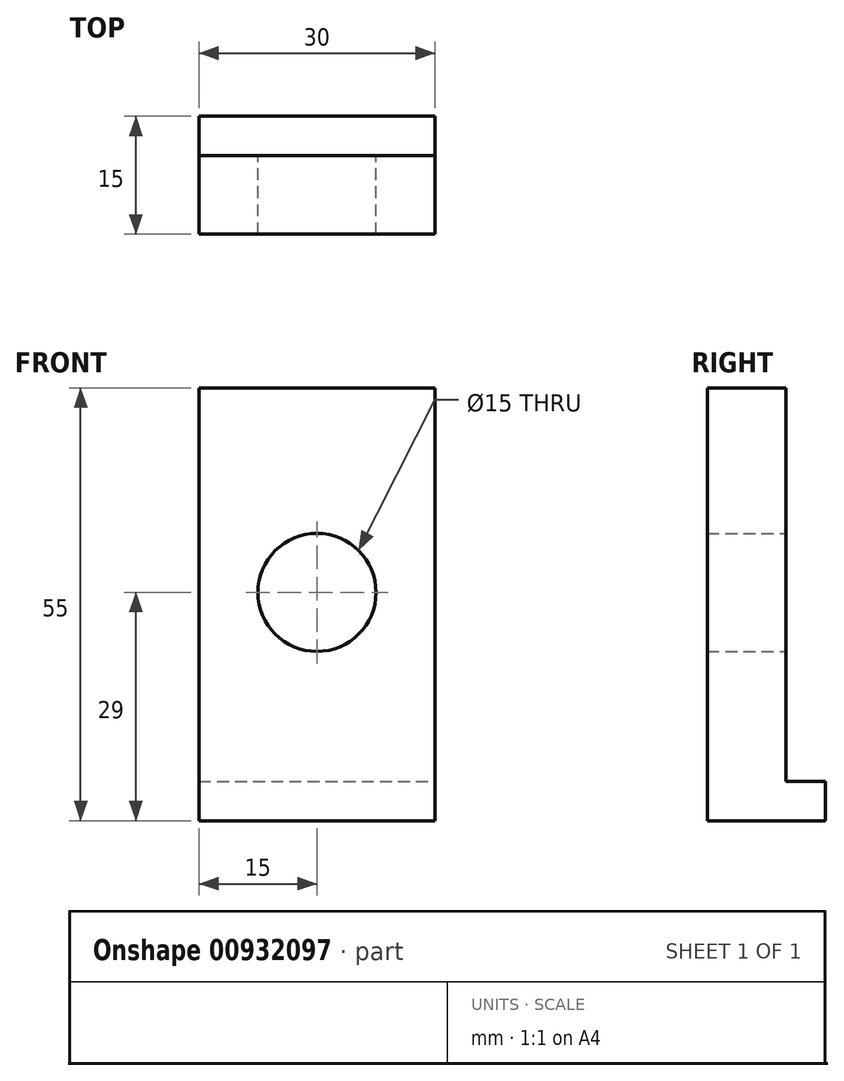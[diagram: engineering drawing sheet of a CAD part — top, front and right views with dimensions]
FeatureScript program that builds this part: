
annotation { "Feature Type Name" : "Feature", "Feature Type Description" : "" }
export const myFeature = defineFeature(function(context is Context, id is Id, definition is map)
    precondition{}
    {
        {
            var Q0;
            Q0=qCreatedBy(makeId("Front.planeOp"),FACE);
            var sketch = newSketch(context, id + "F0", { "sketchPlane" : qUnion([Q0])});
            skLineSegment(sketch, "E0.bottom", {"start": v(15, -25) * mm, "end": v(-15, -25) * mm});
            skLineSegment(sketch, "E0.top", {"start": v(15, 25) * mm, "end": v(-15, 25) * mm});
            skLineSegment(sketch, "E0.left", {"start": v(15, -25) * mm, "end": v(15, 25) * mm});
            skLineSegment(sketch, "E0.right", {"start": v(-15, -25) * mm, "end": v(-15, 25) * mm});
            skPoint(sketch, "E0.middle", {"position": v(0, 0) * mm});
            skCircle(sketch, "E1", {"center": v(0, -1) * mm, "radius": 7.5 * mm});
            skLineSegment(sketch, "E2", {"start": v(-15, -25) * mm, "end": v(-15, -30) * mm});
            skLineSegment(sketch, "E3", {"start": v(-15, -30) * mm, "end": v(15, -30) * mm});
            skLineSegment(sketch, "E4", {"start": v(15, -30) * mm, "end": v(15, -25) * mm});
            skSolve(sketch);
        }
        {
            var Q0;
            Q0=makeQuery(id+"F0.imprint","IMPRINT",FACE,{"disambiguationData":[TD([[makeQuery(id+"F0.imprint","IMPRINT",EDGE,{"derivedFrom":sQuery(id+"F0.wireOp",EDGE,"E0.bottom")}),-1.0]])]});
            var Q1;
            Q1=makeQuery(id+"F0.imprint","IMPRINT",FACE,{"disambiguationData":[TD([[makeQuery(id+"F0.imprint","IMPRINT",EDGE,{"derivedFrom":sQuery(id+"F0.wireOp",EDGE,"E0.bottom")}),1.0]])]});
            var Q2;
            Q2 = qSketchRegion(id + "F2", true);
            extrude(context, id + "F1", {"entities" : qUnion([Q0, Q1, Q2]), "depth" : 10 * mm, "offsetDistance" : 25.4 * mm});
        }
        {
            var Q0;
            Q0=makeQuery(id+"F1.opExtrude","CAP_FACE",FACE,{"disambiguationData":[OSD([sQuery(id+"F0.wireOp",EDGE,"E0.bottom"),sQuery(id+"F0.wireOp",EDGE,"E0.top"),sQuery(id+"F0.wireOp",EDGE,"E0.left"),sQuery(id+"F0.wireOp",EDGE,"E0.right"),sQuery(id+"F0.wireOp",EDGE,"E1")])],"isStart":true});
            var sketch = newSketch(context, id + "F2", { "sketchPlane" : qUnion([Q0])});
            skLineSegment(sketch, "E5.bottom", {"start": v(15, -30) * mm, "end": v(-15, -30) * mm});
            skLineSegment(sketch, "E5.top", {"start": v(15, -25) * mm, "end": v(-15, -25) * mm});
            skLineSegment(sketch, "E5.left", {"start": v(15, -30) * mm, "end": v(15, -25) * mm});
            skLineSegment(sketch, "E5.right", {"start": v(-15, -30) * mm, "end": v(-15, -25) * mm});
            skSolve(sketch);
        }
        {
            var Q0;
            Q0 = qSketchRegion(id + "F2", true);
            var Q1;
            Q1=makeQuery(id+"F1.opExtrude","CAP_FACE",FACE,{"disambiguationData":[OSD([sQuery(id+"F0.wireOp",EDGE,"E0.top"),sQuery(id+"F0.wireOp",EDGE,"E0.left"),sQuery(id+"F0.wireOp",EDGE,"E0.right"),sQuery(id+"F0.wireOp",EDGE,"E1"),sQuery(id+"F0.wireOp",EDGE,"E2"),sQuery(id+"F0.wireOp",EDGE,"E3"),sQuery(id+"F0.wireOp",EDGE,"E4")])],"isStart":false});
            extrude(context, id + "F3", {"entities" : qUnion([Q0, Q1]), "operationType" : NewBodyOperationType.ADD, "depth" : 5 * mm, "offsetDistance" : 25.4 * mm});
        }
    });
